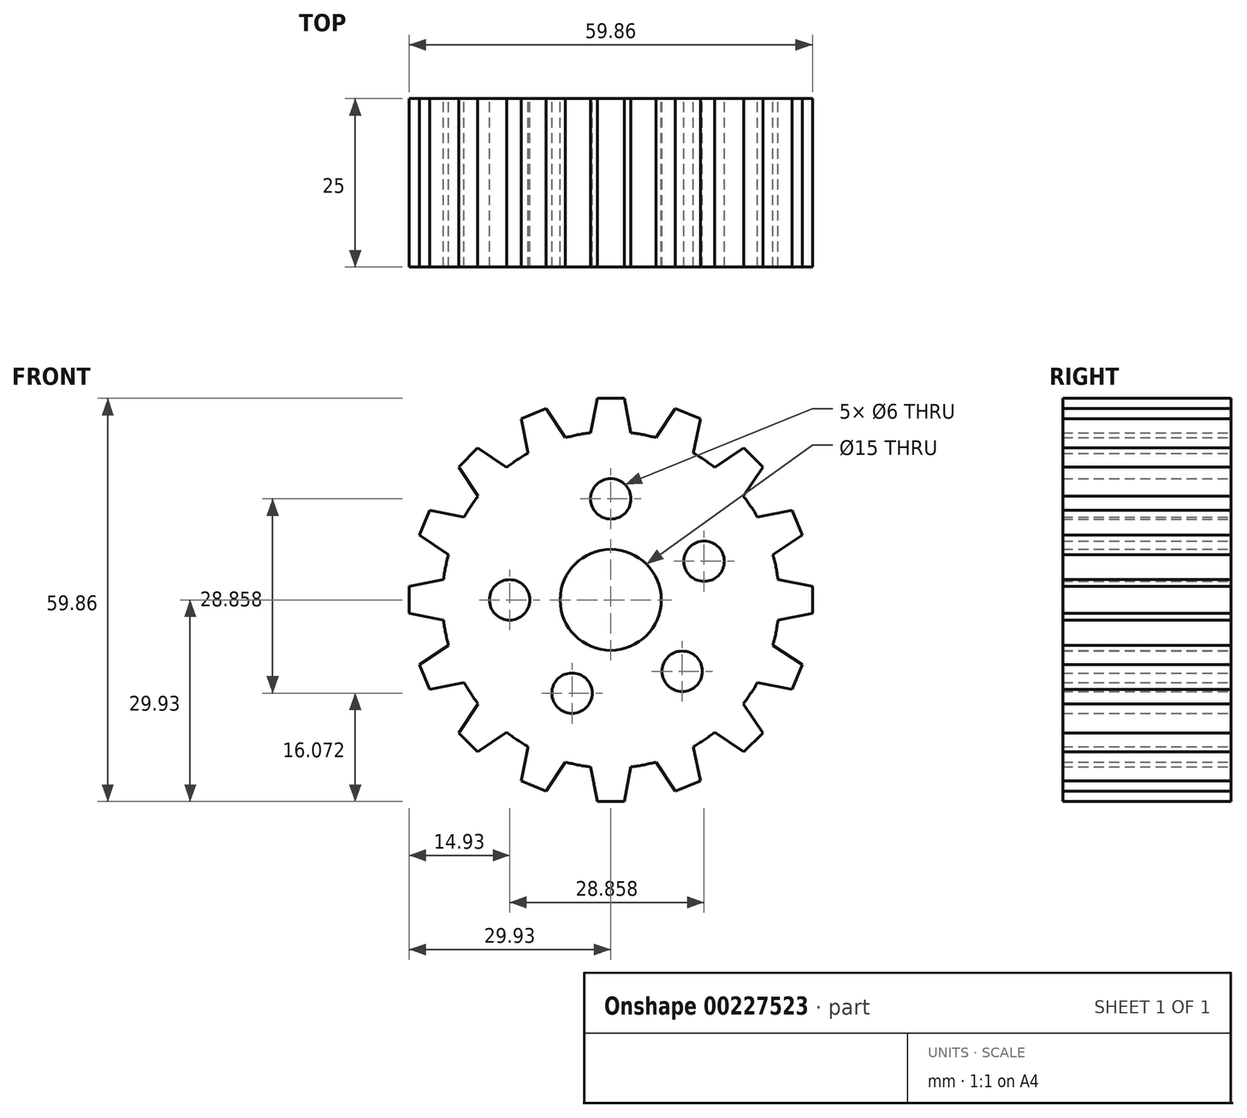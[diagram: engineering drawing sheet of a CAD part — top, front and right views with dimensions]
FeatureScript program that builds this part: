
annotation { "Feature Type Name" : "Feature", "Feature Type Description" : "" }
export const myFeature = defineFeature(function(context is Context, id is Id, definition is map)
    precondition{}
    {
        {
            var Q0;
            Q0=qCreatedBy(makeId("Front.planeOp"),FACE);
            var sketch = newSketch(context, id + "F0", { "sketchPlane" : qUnion([Q0])});
            skLineSegment(sketch, "E0", {"start": v(0, 0) * mm, "end": v(0, 31.37) * mm, "construction": true});
            skLineSegment(sketch, "E1", {"start": v(0, 0) * mm, "end": v(-30.86, 0) * mm, "construction": true});
            skCircle(sketch, "E2", {"center": v(0, 0) * mm, "radius": 7.5 * mm});
            skCircle(sketch, "E3", {"center": v(0, 0) * mm, "radius": 25 * mm});
            skCircle(sketch, "E4", {"center": v(0, 0) * mm, "radius": 15 * mm, "construction": true});
            skLineSegment(sketch, "E5", {"start": v(-2, 29.93) * mm, "end": v(-3, 24.82) * mm});
            skLineSegment(sketch, "E6", {"start": v(2, 29.93) * mm, "end": v(3, 24.82) * mm});
            skLineSegment(sketch, "E7", {"start": v(-2, 29.93) * mm, "end": v(2, 29.93) * mm});
            skPoint(sketch, "E8", {"position": v(0, 29.93) * mm});
            skLineSegment(sketch, "E9.1.0", {"start": v(-13.3, 26.89) * mm, "end": v(-12.27, 21.78) * mm});
            skLineSegment(sketch, "E9.1.1", {"start": v(-13.3, 26.89) * mm, "end": v(-9.6, 28.42) * mm});
            skLineSegment(sketch, "E9.1.2", {"start": v(-9.6, 28.42) * mm, "end": v(-6.73, 24.08) * mm});
            skLineSegment(sketch, "E9.2.0", {"start": v(-22.58, 19.75) * mm, "end": v(-19.67, 15.43) * mm});
            skLineSegment(sketch, "E9.2.1", {"start": v(-22.58, 19.75) * mm, "end": v(-19.75, 22.58) * mm});
            skLineSegment(sketch, "E9.2.2", {"start": v(-19.75, 22.58) * mm, "end": v(-15.43, 19.67) * mm});
            skLineSegment(sketch, "E9.3.0", {"start": v(-28.42, 9.6) * mm, "end": v(-24.08, 6.73) * mm});
            skLineSegment(sketch, "E9.3.1", {"start": v(-28.42, 9.6) * mm, "end": v(-26.89, 13.3) * mm});
            skLineSegment(sketch, "E9.3.2", {"start": v(-26.89, 13.3) * mm, "end": v(-21.78, 12.27) * mm});
            skLineSegment(sketch, "E9.4.0", {"start": v(-29.93, -2) * mm, "end": v(-24.82, -3) * mm});
            skLineSegment(sketch, "E9.4.1", {"start": v(-29.93, -2) * mm, "end": v(-29.93, 2) * mm});
            skLineSegment(sketch, "E9.4.2", {"start": v(-29.93, 2) * mm, "end": v(-24.82, 3) * mm});
            skLineSegment(sketch, "E9.5.0", {"start": v(-26.89, -13.3) * mm, "end": v(-21.78, -12.27) * mm});
            skLineSegment(sketch, "E9.5.1", {"start": v(-26.89, -13.3) * mm, "end": v(-28.42, -9.6) * mm});
            skLineSegment(sketch, "E9.5.2", {"start": v(-28.42, -9.6) * mm, "end": v(-24.08, -6.73) * mm});
            skLineSegment(sketch, "E9.6.0", {"start": v(-19.75, -22.58) * mm, "end": v(-15.43, -19.67) * mm});
            skLineSegment(sketch, "E9.6.1", {"start": v(-19.75, -22.58) * mm, "end": v(-22.58, -19.75) * mm});
            skLineSegment(sketch, "E9.6.2", {"start": v(-22.58, -19.75) * mm, "end": v(-19.67, -15.43) * mm});
            skLineSegment(sketch, "E9.7.0", {"start": v(-9.6, -28.42) * mm, "end": v(-6.73, -24.08) * mm});
            skLineSegment(sketch, "E9.7.1", {"start": v(-9.6, -28.42) * mm, "end": v(-13.3, -26.89) * mm});
            skLineSegment(sketch, "E9.7.2", {"start": v(-13.3, -26.89) * mm, "end": v(-12.27, -21.78) * mm});
            skLineSegment(sketch, "E9.8.0", {"start": v(2, -29.93) * mm, "end": v(3, -24.82) * mm});
            skLineSegment(sketch, "E9.8.1", {"start": v(2, -29.93) * mm, "end": v(-2, -29.93) * mm});
            skLineSegment(sketch, "E9.8.2", {"start": v(-2, -29.93) * mm, "end": v(-3, -24.82) * mm});
            skLineSegment(sketch, "E9.9.0", {"start": v(13.3, -26.89) * mm, "end": v(12.27, -21.78) * mm});
            skLineSegment(sketch, "E9.9.1", {"start": v(13.3, -26.89) * mm, "end": v(9.6, -28.42) * mm});
            skLineSegment(sketch, "E9.9.2", {"start": v(9.6, -28.42) * mm, "end": v(6.73, -24.08) * mm});
            skLineSegment(sketch, "E9.10.0", {"start": v(22.58, -19.75) * mm, "end": v(19.67, -15.43) * mm});
            skLineSegment(sketch, "E9.10.1", {"start": v(22.58, -19.75) * mm, "end": v(19.75, -22.58) * mm});
            skLineSegment(sketch, "E9.10.2", {"start": v(19.75, -22.58) * mm, "end": v(15.43, -19.67) * mm});
            skLineSegment(sketch, "E9.11.0", {"start": v(28.42, -9.6) * mm, "end": v(24.08, -6.73) * mm});
            skLineSegment(sketch, "E9.11.1", {"start": v(28.42, -9.6) * mm, "end": v(26.89, -13.3) * mm});
            skLineSegment(sketch, "E9.11.2", {"start": v(26.89, -13.3) * mm, "end": v(21.78, -12.27) * mm});
            skLineSegment(sketch, "E9.12.0", {"start": v(29.93, 2) * mm, "end": v(24.82, 3) * mm});
            skLineSegment(sketch, "E9.12.1", {"start": v(29.93, 2) * mm, "end": v(29.93, -2) * mm});
            skLineSegment(sketch, "E9.12.2", {"start": v(29.93, -2) * mm, "end": v(24.82, -3) * mm});
            skLineSegment(sketch, "E9.13.0", {"start": v(26.89, 13.3) * mm, "end": v(21.78, 12.27) * mm});
            skLineSegment(sketch, "E9.13.1", {"start": v(26.89, 13.3) * mm, "end": v(28.42, 9.6) * mm});
            skLineSegment(sketch, "E9.13.2", {"start": v(28.42, 9.6) * mm, "end": v(24.08, 6.73) * mm});
            skLineSegment(sketch, "E9.14.0", {"start": v(19.75, 22.58) * mm, "end": v(15.43, 19.67) * mm});
            skLineSegment(sketch, "E9.14.1", {"start": v(19.75, 22.58) * mm, "end": v(22.58, 19.75) * mm});
            skLineSegment(sketch, "E9.14.2", {"start": v(22.58, 19.75) * mm, "end": v(19.67, 15.43) * mm});
            skLineSegment(sketch, "E9.15.0", {"start": v(9.6, 28.42) * mm, "end": v(6.73, 24.08) * mm});
            skLineSegment(sketch, "E9.15.1", {"start": v(9.6, 28.42) * mm, "end": v(13.3, 26.89) * mm});
            skLineSegment(sketch, "E9.15.2", {"start": v(13.3, 26.89) * mm, "end": v(12.27, 21.78) * mm});
            skCircle(sketch, "E10", {"center": v(0, 15) * mm, "radius": 3 * mm});
            skCircle(sketch, "E11.1.0", {"center": v(13.86, 5.74) * mm, "radius": 3 * mm});
            skCircle(sketch, "E11.2.0", {"center": v(10.6, -10.6) * mm, "radius": 3 * mm});
            skCircle(sketch, "E11.3.0", {"center": v(-5.74, -13.86) * mm, "radius": 3 * mm});
            skCircle(sketch, "E11.4.0", {"center": v(-15, 0) * mm, "radius": 3 * mm});
            skLineSegment(sketch, "E11.anchor1", {"start": v(0, 0) * mm, "end": v(0, 15) * mm, "construction": true});
            skLineSegment(sketch, "E11.anchor2", {"start": v(0, 0) * mm, "end": v(-15, 0) * mm, "construction": true});
            skSolve(sketch);
        }
        {
            var Q0;
            Q0 = qSketchRegion(id + "F0", true);
            extrude(context, id + "F1", {"entities" : qUnion([Q0]), "depth" : 25 * mm});
        }
    });
